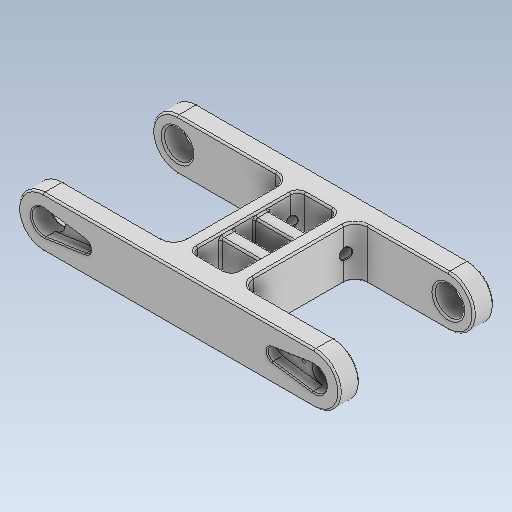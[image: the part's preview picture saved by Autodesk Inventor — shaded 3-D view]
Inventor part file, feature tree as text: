
AUTODESK INVENTOR PART (.ipt)
format: ipt  version: 2020.3 (Build 243373000, 373)  size: 427,008 bytes
history: native  units: mm
features: sketch x7, other x3
ambient origin geometry x8: Origin, YZ Plane, XZ Plane, XY Plane, X Axis, Y Axis, Z Axis, Center Point
bodies: Solid1 (feature_tree)
feature tree (10):
  other  "LegMiddle_Final_1.ipt"
  other  "Solid1::LegMiddle_Final_1.ipt"
  other  "TaggingFeature1"
  sketch  "Sketch1"  dims[d0=10.0mm]
  sketch  "Sketch2"
  sketch  "Sketch5"
  sketch  "Sketch14"
  sketch  "Sketch6"
  sketch  "Sketch12"
  sketch  "Sketch13"
